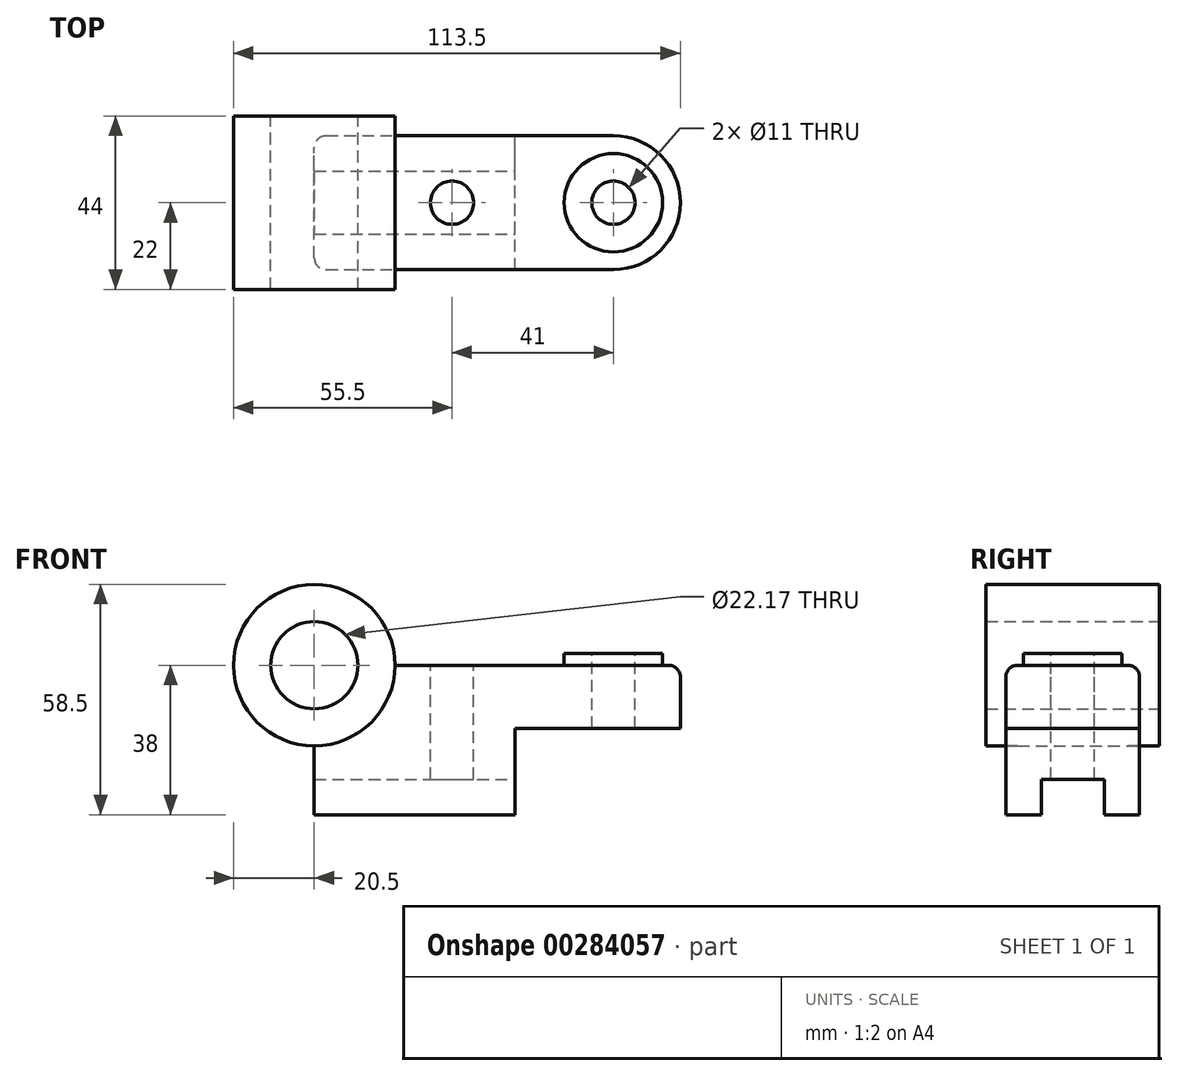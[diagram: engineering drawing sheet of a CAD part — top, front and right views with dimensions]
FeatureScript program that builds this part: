
annotation { "Feature Type Name" : "Feature", "Feature Type Description" : "" }
export const myFeature = defineFeature(function(context is Context, id is Id, definition is map)
    precondition{}
    {
        {
            var Q0;
            Q0=qCreatedBy(makeId("Front.planeOp"),FACE);
            var sketch = newSketch(context, id + "F0", { "sketchPlane" : qUnion([Q0])});
            skLineSegment(sketch, "E0.bottom", {"start": v(0, 0) * mm, "end": v(51, 0) * mm});
            skLineSegment(sketch, "E0.top", {"start": v(11.08, 38) * mm, "end": v(76, 38) * mm});
            skLineSegment(sketch, "E0.left", {"start": v(0, 0) * mm, "end": v(0, 26.92) * mm});
            skLineSegment(sketch, "E0.right", {"start": v(76, 22) * mm, "end": v(76, 38) * mm});
            skLineSegment(sketch, "E1.top", {"start": v(76, 22) * mm, "end": v(51, 22) * mm});
            skLineSegment(sketch, "E1.right", {"start": v(51, 0) * mm, "end": v(51, 22) * mm});
            skCircle(sketch, "E2", {"center": v(0, 38) * mm, "radius": 11.09 * mm});
            skCircle(sketch, "E3", {"center": v(0, 38) * mm, "radius": 20.5 * mm});
            skSolve(sketch);
        }
        {
            var Q0;
            {var subQ2=sQuery(id+"F0.wireOp",EDGE,"E0.bottom");Q0=makeQuery(id+"F0.imprint","IMPRINT",FACE,{"disambiguationData":[TD([[makeQuery(id+"F0.imprint","IMPRINT",EDGE,{"derivedFrom":subQ2}),1.0]])]});}
            extrude(context, id + "F1", {"entities" : qUnion([Q0]), "endBound" : BoundingType.SYMMETRIC, "depth" : 17 * 2 * mm});
        }
        {
            var Q0;
            {var subQ0=sQuery(id+"F0.wireOp",EDGE,"E2");var subQ1=sQuery(id+"F0.wireOp",EDGE,"E0.top");var subQ2=makeQuery(id+"F0.imprint","INTERSECT",VERTEX,{"derivedFrom":[subQ1,subQ0]});Q0=makeQuery(id+"F0.imprint","IMPRINT",FACE,{"disambiguationData":[TD([[makeQuery(id+"F0.imprint","IMPRINT",EDGE,{"disambiguationData":[TD([[subQ2,-1.0]])],"derivedFrom":subQ1}),1.0]])]});}
            var Q1;
            {var subQ0=sQuery(id+"F0.wireOp",EDGE,"E2");var subQ1=sQuery(id+"F0.wireOp",EDGE,"E0.top");var subQ2=makeQuery(id+"F0.imprint","INTERSECT",VERTEX,{"derivedFrom":[subQ1,subQ0]});Q1=makeQuery(id+"F0.imprint","IMPRINT",FACE,{"disambiguationData":[TD([[makeQuery(id+"F0.imprint","IMPRINT",EDGE,{"disambiguationData":[TD([[subQ2,-1.0]])],"derivedFrom":subQ1}),-1.0]])]});}
            extrude(context, id + "F2", {"entities" : qUnion([Q0, Q1]), "operationType" : NewBodyOperationType.ADD, "endBound" : BoundingType.SYMMETRIC, "depth" : 44 * mm});
        }
        {
            var Q0;
            Q0=makeQuery(id+"F1.opExtrude","SWEPT_FACE",FACE,{"disambiguationData":[OSD([sQuery(id+"F0.wireOp",EDGE,"E0.top")])]});
            var sketch = newSketch(context, id + "F3", { "sketchPlane" : qUnion([Q0])});
            skArc(sketch, "E4", {"start": v(76, -17) * mm, "mid": v(93, 0) * mm, "end": v(76, 17) * mm});
            skSolve(sketch);
        }
        {
            var Q0;
            Q0=makeQuery(id+"F3.imprint","IMPRINT",FACE,{"disambiguationData":[TD([[makeQuery(id+"F3.imprint","IMPRINT",EDGE,{"derivedFrom":sQuery(id+"F3.wireOp",EDGE,"E4")}),1.0]])]});
            var Q1;
            Q1=makeQuery(id+"F1.opExtrude","SWEPT_FACE",FACE,{"disambiguationData":[OSD([sQuery(id+"F0.wireOp",EDGE,"E1.top")])]});
            extrude(context, id + "F4", {"entities" : qUnion([Q0]), "operationType" : NewBodyOperationType.ADD, "endBound" : BoundingType.UP_TO_SURFACE, "oppositeDirection" : true, "endBoundEntityFace" : qUnion([Q1]), "depth" : 25 * mm});
        }
        {
            var Q0;
            {var subQ0=sQuery(id+"F0.wireOp",EDGE,"E0.top");Q0=makeQuery(id+"F4.boolean.opBoolean","MERGE",FACE,{"derivedFrom":[makeQuery(id+"F1.opExtrude","SWEPT_FACE",FACE,{"disambiguationData":[OSD([subQ0])]}),makeQuery(id+"F4.opExtrude","CAP_FACE",FACE,{"disambiguationData":[OSD([subQ0,sQuery(id+"F0.wireOp",EDGE,"E0.right"),sQuery(id+"F3.wireOp",EDGE,"E4")])],"isStart":true})]});}
            var sketch = newSketch(context, id + "F5", { "sketchPlane" : qUnion([Q0])});
            skCircle(sketch, "E5", {"center": v(76, 0) * mm, "radius": 12.5 * mm});
            skSolve(sketch);
        }
        {
            var Q0;
            Q0 = qSketchRegion(id + "F5", true);
            extrude(context, id + "F6", {"entities" : qUnion([Q0]), "operationType" : NewBodyOperationType.ADD, "depth" : 3 * mm});
        }
        {
            var Q0;
            Q0=makeQuery(id+"F6.opExtrude","CAP_FACE",FACE,{"disambiguationData":[OSD([sQuery(id+"F5.wireOp",EDGE,"E5")])],"isStart":false});
            var sketch = newSketch(context, id + "F7", { "sketchPlane" : qUnion([Q0])});
            skCircle(sketch, "E6", {"center": v(76, 0) * mm, "radius": 5.5 * mm});
            skSolve(sketch);
        }
        {
            var Q0;
            Q0 = qSketchRegion(id + "F7", true);
            extrude(context, id + "F8", {"entities" : qUnion([Q0]), "operationType" : NewBodyOperationType.REMOVE, "endBound" : BoundingType.THROUGH_ALL, "oppositeDirection" : true, "depth" : 25 * mm});
        }
        {
            var Q0;
            {var subQ0=sQuery(id+"F0.wireOp",EDGE,"E0.top");Q0=makeQuery(id+"F4.boolean.opBoolean","MERGE",FACE,{"derivedFrom":[makeQuery(id+"F1.opExtrude","SWEPT_FACE",FACE,{"disambiguationData":[OSD([subQ0])]}),makeQuery(id+"F4.opExtrude","CAP_FACE",FACE,{"disambiguationData":[OSD([subQ0,sQuery(id+"F0.wireOp",EDGE,"E0.right"),sQuery(id+"F3.wireOp",EDGE,"E4")])],"isStart":true})]});}
            var sketch = newSketch(context, id + "F9", { "sketchPlane" : qUnion([Q0])});
            skCircle(sketch, "E7", {"center": v(35, 0) * mm, "radius": 5.5 * mm});
            skSolve(sketch);
        }
        {
            var Q0;
            Q0 = qSketchRegion(id + "F9", true);
            extrude(context, id + "F10", {"entities" : qUnion([Q0]), "operationType" : NewBodyOperationType.REMOVE, "endBound" : BoundingType.THROUGH_ALL, "oppositeDirection" : true, "depth" : 25 * mm});
        }
        {
            var Q0;
            Q0=makeQuery(id+"F1.opExtrude","SWEPT_FACE",FACE,{"disambiguationData":[OSD([sQuery(id+"F0.wireOp",EDGE,"E1.right")])]});
            var sketch = newSketch(context, id + "F11", { "sketchPlane" : qUnion([Q0])});
            skLineSegment(sketch, "E8.bottom", {"start": v(-8, 0) * mm, "end": v(8, 0) * mm});
            skLineSegment(sketch, "E8.top", {"start": v(-8, 9) * mm, "end": v(8, 9) * mm});
            skLineSegment(sketch, "E8.left", {"start": v(-8, 0) * mm, "end": v(-8, 9) * mm});
            skLineSegment(sketch, "E8.right", {"start": v(8, 0) * mm, "end": v(8, 9) * mm});
            skSolve(sketch);
        }
        {
            var Q0;
            Q0 = qSketchRegion(id + "F11", true);
            extrude(context, id + "F12", {"entities" : qUnion([Q0]), "operationType" : NewBodyOperationType.REMOVE, "endBound" : BoundingType.THROUGH_ALL, "oppositeDirection" : true, "depth" : 25 * mm});
        }
        {
            var Q0;
            Q0=makeQuery(id+"F6.opExtrude","CAP_EDGE",EDGE,{"disambiguationData":[OSD([sQuery(id+"F5.wireOp",EDGE,"E5")])],"isStart":true});
            var Q1;
            Q1=makeQuery(id+"F1.opExtrude","SWEPT_EDGE",EDGE,{"disambiguationData":[OSD([sQuery(id+"F0.wireOp",EDGE,"E0.top"),sQuery(id+"F0.wireOp",EDGE,"E3")])]});
            var Q2;
            Q2=makeQuery(id+"F1.opExtrude","CAP_EDGE",EDGE,{"disambiguationData":[OSD([sQuery(id+"F0.wireOp",EDGE,"E3")])],"isStart":false});
            var Q3;
            Q3=makeQuery(id+"F1.opExtrude","CAP_EDGE",EDGE,{"disambiguationData":[OSD([sQuery(id+"F0.wireOp",EDGE,"E0.left")])],"isStart":false});
            var Q4;
            Q4=makeQuery(id+"F1.opExtrude","CAP_EDGE",EDGE,{"disambiguationData":[OSD([sQuery(id+"F0.wireOp",EDGE,"E0.left")])],"isStart":true});
            fillet(context, id + "F13", {"entities" : qUnion([Q0, Q1, Q2, Q3, Q4]), "radius" : 3 * mm, "tangentPropagation" : true, "allowEdgeOverflow" : false});
        }
        {
            var Q0;
            Q0=makeQuery(id+"F1.opExtrude","CAP_EDGE",EDGE,{"disambiguationData":[OSD([sQuery(id+"F0.wireOp",EDGE,"E0.top")])],"isStart":false});
            fillet(context, id + "F14", {"entities" : qUnion([Q0]), "radius" : 3 * mm, "tangentPropagation" : true, "allowEdgeOverflow" : false});
        }
    });
